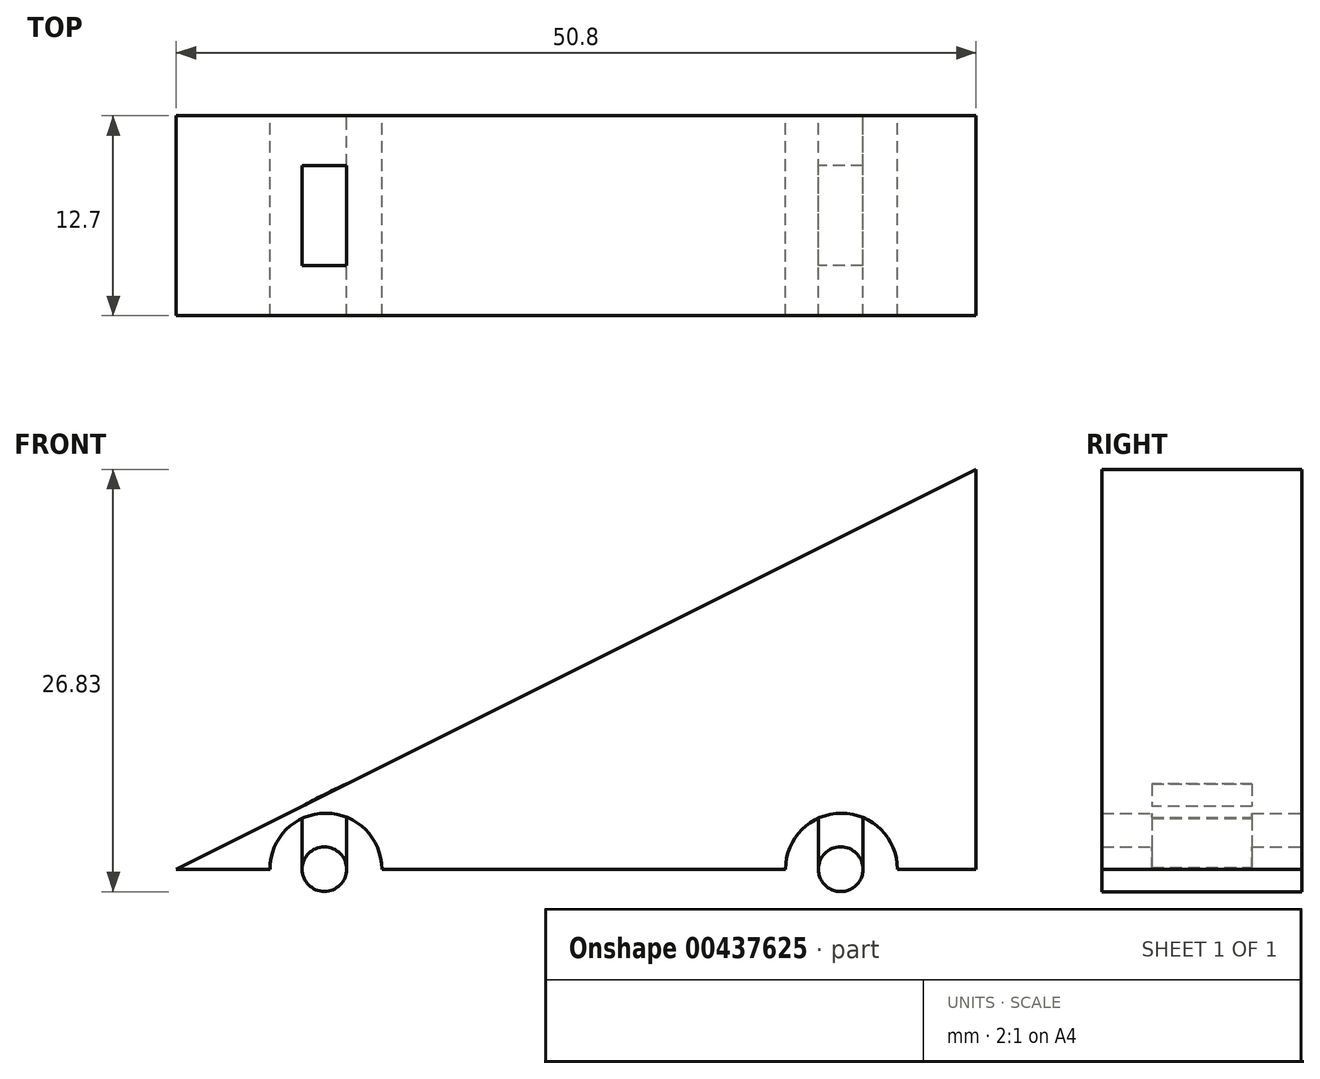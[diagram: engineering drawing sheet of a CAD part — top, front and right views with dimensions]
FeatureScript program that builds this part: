
annotation { "Feature Type Name" : "Feature", "Feature Type Description" : "" }
export const myFeature = defineFeature(function(context is Context, id is Id, definition is map)
    precondition{}
    {
        {
            var Q0;
            Q0=qCreatedBy(makeId("Front.planeOp"),FACE);
            var sketch = newSketch(context, id + "F0", { "sketchPlane" : qUnion([Q0])});
            skLineSegment(sketch, "E0", {"start": v(17.3, 25.4) * mm, "end": v(17.3, 0) * mm});
            skLineSegment(sketch, "E1", {"start": v(17.3, 0) * mm, "end": v(-33.5, 0) * mm});
            skCircle(sketch, "E2", {"center": v(-23.99, 0) * mm, "radius": 3.55 * mm});
            skCircle(sketch, "E3", {"center": v(8.76, 0) * mm, "radius": 3.55 * mm});
            skLineSegment(sketch, "E4", {"start": v(17.3, 25.4) * mm, "end": v(-33.5, 0) * mm});
            skSolve(sketch);
        }
        {
            var Q0;
            {var subQ5=sQuery(id+"F0.wireOp",EDGE,"E0");Q0=makeQuery(id+"F0.imprint","IMPRINT",FACE,{"disambiguationData":[TD([[makeQuery(id+"F0.imprint","IMPRINT",EDGE,{"derivedFrom":subQ5}),-1.0]])]});}
            extrude(context, id + "F1", {"entities" : qUnion([Q0]), "endBound" : BoundingType.SYMMETRIC, "depth" : 12.7 * mm});
        }
        {
            var Q0;
            Q0=qCreatedBy(makeId("Front.planeOp"),FACE);
            var sketch = newSketch(context, id + "F2", { "sketchPlane" : qUnion([Q0])});
            skLineSegment(sketch, "E5.bottom", {"start": v(-25.5, 10.48) * mm, "end": v(-22.66, 10.48) * mm});
            skLineSegment(sketch, "E5.top", {"start": v(-25.5, 0) * mm, "end": v(-22.66, 0) * mm});
            skLineSegment(sketch, "E5.left", {"start": v(-25.5, 10.48) * mm, "end": v(-25.5, 0) * mm});
            skLineSegment(sketch, "E5.right", {"start": v(-22.66, 10.48) * mm, "end": v(-22.66, 0) * mm});
            skPoint(sketch, "E6.right.end.orphan", {"position": v(10.48, 0) * mm});
            skPoint(sketch, "E6.bottom.start.orphan", {"position": v(6.8, 10.48) * mm});
            skLineSegment(sketch, "E7.left", {"start": v(7.3, 10.48) * mm, "end": v(7.3, 0) * mm});
            skLineSegment(sketch, "E7.right", {"start": v(10.13, 10.48) * mm, "end": v(10.13, 0) * mm});
            skLineSegment(sketch, "E8", {"start": v(7.3, 10.48) * mm, "end": v(10.13, 10.48) * mm});
            skLineSegment(sketch, "E9", {"start": v(7.3, 0) * mm, "end": v(10.13, 0) * mm});
            skSolve(sketch);
        }
        {
            var Q0;
            Q0=makeQuery(id+"F2.imprint","IMPRINT",FACE,{"disambiguationData":[TD([[makeQuery(id+"F2.imprint","IMPRINT",EDGE,{"derivedFrom":sQuery(id+"F2.wireOp",EDGE,"E5.bottom")}),-1.0]])]});
            var Q1;
            Q1=makeQuery(id+"F2.imprint","IMPRINT",FACE,{"disambiguationData":[TD([[makeQuery(id+"F2.imprint","IMPRINT",EDGE,{"derivedFrom":sQuery(id+"F2.wireOp",EDGE,"E6.bottom")}),-1.0]])]});
            var Q2;
            Q2=makeQuery(id+"F2.imprint","IMPRINT",FACE,{"disambiguationData":[TD([[makeQuery(id+"F2.imprint","IMPRINT",EDGE,{"derivedFrom":sQuery(id+"F2.wireOp",EDGE,"E7.left")}),1.0]])]});
            extrude(context, id + "F3", {"entities" : qUnion([Q0, Q1, Q2]), "operationType" : NewBodyOperationType.ADD, "endBound" : BoundingType.SYMMETRIC, "depth" : 6.35 * mm});
        }
        {
            var Q0;
            Q0=makeQuery(id+"F3.opExtrude","SWEPT_EDGE",EDGE,{"disambiguationData":[OSD([sQuery(id+"F2.wireOp",EDGE,"E5.bottom"),sQuery(id+"F2.wireOp",EDGE,"E5.left")])]});
            fillet(context, id + "F4", {"entities" : qUnion([Q0]), "radius" : 54.08 * mm, "tangentPropagation" : true, "allowEdgeOverflow" : false});
        }
        {
            var Q0;
            Q0=qCreatedBy(makeId("Front.planeOp"),FACE);
            var sketch = newSketch(context, id + "F5", { "sketchPlane" : qUnion([Q0])});
            skArc(sketch, "E10", {"start": v(-22.67, 0) * mm, "mid": v(-24.08, 1.41) * mm, "end": v(-25.5, 0) * mm});
            skArc(sketch, "E11", {"start": v(-25.5, 0) * mm, "mid": v(-24.08, -1.41) * mm, "end": v(-22.67, 0) * mm});
            skArc(sketch, "E12", {"start": v(10.13, 0) * mm, "mid": v(8.71, 1.42) * mm, "end": v(7.3, 0) * mm});
            skArc(sketch, "E13", {"start": v(7.3, 0) * mm, "mid": v(8.71, -1.43) * mm, "end": v(10.13, 0) * mm});
            skSolve(sketch);
        }
        {
            var Q0;
            Q0=makeQuery(id+"F5.imprint","IMPRINT",FACE,{"disambiguationData":[TD([[makeQuery(id+"F5.imprint","IMPRINT",EDGE,{"derivedFrom":sQuery(id+"F5.wireOp",EDGE,"E10")}),1.0]])]});
            var Q1;
            Q1=makeQuery(id+"F5.imprint","IMPRINT",FACE,{"disambiguationData":[TD([[makeQuery(id+"F5.imprint","IMPRINT",EDGE,{"derivedFrom":sQuery(id+"F5.wireOp",EDGE,"E12")}),1.0]])]});
            extrude(context, id + "F6", {"entities" : qUnion([Q0, Q1]), "operationType" : NewBodyOperationType.ADD, "endBound" : BoundingType.SYMMETRIC, "depth" : 12.7 * mm});
        }
    });
